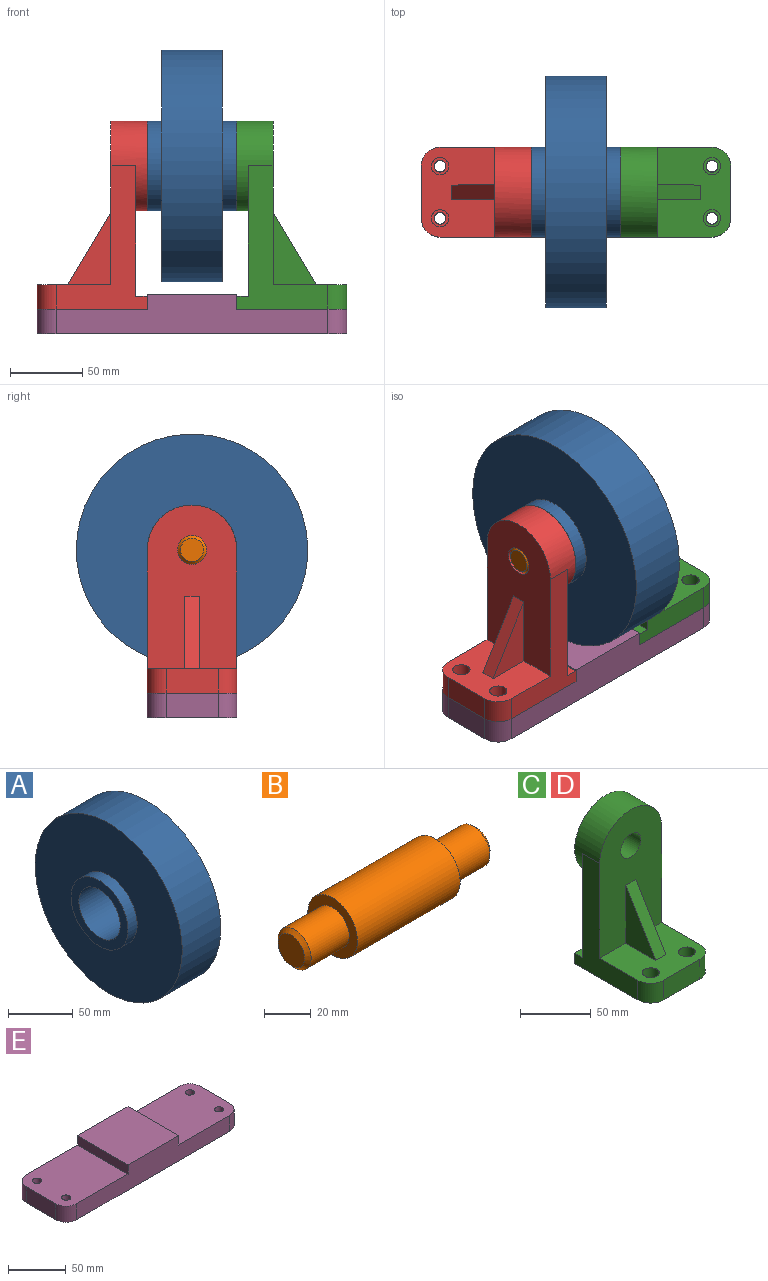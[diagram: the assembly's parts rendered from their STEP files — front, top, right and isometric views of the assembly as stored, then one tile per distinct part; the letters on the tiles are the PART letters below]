
ASSEMBLY  parts=5 mates=4
PART A: 8 faces, bbox 62x160x160 mm
  f0: cylinder r=31mm len=62mm, axis (-1,0,0), area 1947.8mm2, adj f4,f7
  f1: cylinder r=22.5mm len=62mm, axis (-1,0,0), area 8765mm2, adj f3,f4
  f2: cylinder r=31mm len=62mm, axis (-1,0,0), area 1947.8mm2, adj f3,f6
  f3: plane 62x62mm, normal (1,0,0), area 1428.6mm2, adj f1,f2
  f4: plane 62x62mm, normal (-1,0,0), area 1428.6mm2, adj f0,f1
  f5: cylinder r=80mm len=160mm, axis (-1,0,0), area 21111.5mm2, adj f6,f7
  f6: plane 160x160mm, normal (1,0,0), area 17087.1mm2, adj f2,f5
  f7: plane 160x160mm, normal (-1,0,0), area 17087.1mm2, adj f0,f5
PART B: 9 faces, bbox 112x30x30 mm
  f0: cylinder r=10mm len=23mm, axis (-1,0,0), area 1445.1mm2, adj f3,f8
  f1: plane 16x16mm, normal (1,0,0), area 201.1mm2, adj f8
  f2: cylinder r=15mm len=62mm, axis (-1,0,0), area 5843.4mm2, adj f3,f4
  f3: plane 30x30mm, normal (1,0,0), area 392.7mm2, adj f0,f2
  f4: plane 30x30mm, normal (-1,0,0), area 392.7mm2, adj f2,f6
  f5: plane 16x16mm, normal (-1,0,0), area 201.1mm2, adj f7
  f6: cylinder r=10mm len=23mm, axis (-1,0,0), area 1445.1mm2, adj f4,f7
  f7: cone r=10mm half-angle=45deg, axis (1,0,0), area 159.9mm2, adj f5,f6
  f8: cone r=8mm half-angle=45deg, axis (-1,0,0), area 159.9mm2, adj f0,f1
PART C: 23 faces, bbox 62x76x130 mm
  f0: cylinder r=4.1mm len=8.2mm, axis (0,0,-1), area 206.1mm2, adj f9,f17
  f1: cylinder r=4.1mm len=8.2mm, axis (0,0,-1), area 206.1mm2, adj f9,f19
  f2: plane 62x9mm, normal (0,1,0), area 558mm2, adj f3,f7,f9,f11
  f3: plane 99x63mm, normal (-1,0,0), area 2401mm2, adj f2,f4,f8,f9,f10,f11,f12,f14
  f4: cylinder r=13mm len=17mm, axis (0,0,-1), area 347.1mm2, adj f3,f5,f8,f9
  f5: plane 36x17mm, normal (0,-1,0), area 612mm2, adj f4,f6,f8,f9
  f6: cylinder r=13mm len=17mm, axis (0,0,-1), area 347.1mm2, adj f5,f7,f8,f9
  f7: plane 99x63mm, normal (1,0,0), area 2401mm2, adj f2,f6,f8,f9,f10,f11,f12,f14
  f8: plane 62x51mm, normal (0,0,1), area 2563.3mm2, adj f3,f4,f5,f6,f7,f12,f16,f18
  f9: plane 76x62mm, normal (0,0,-1), area 4533.8mm2, adj f0,f1,f2,f3,f4,f5,f6,f7
  f10: plane 90x62mm, normal (0,1,0), area 4070.5mm2, adj f3,f7,f11,f14
  f11: plane 62x8mm, normal (0,0,1), area 496mm2, adj f2,f3,f7,f10
  f12: plane 113x62mm, normal (0,-1,0), area 5779.4mm2, adj f3,f7,f8,f13,f14,f20,f21,f22
  f13: cylinder r=10mm len=25mm, axis (0,-1,0), area 1570.8mm2, adj f12,f15
  f14: cylinder r=31mm len=62mm, axis (0,-1,0), area 3213.8mm2, adj f3,f7,f10,f12,f15
  f15: plane 62x62mm, normal (0,1,0), area 2704.9mm2, adj f13,f14
  f16: cylinder r=6mm len=12mm, axis (0,0,1), area 339.3mm2, adj f8,f17
  f17: plane 12x12mm, normal (0,0,1), area 60.3mm2, adj f0,f16
  f18: cylinder r=6mm len=12mm, axis (0,0,1), area 339.3mm2, adj f8,f19
  f19: plane 12x12mm, normal (0,0,1), area 60.3mm2, adj f1,f18
  f20: plane 50x30mm, normal (-1,0,0), area 750mm2, adj f8,f12,f21
  f21: plane 50x30mm, normal (0,-0.86,0.51), area 583.1mm2, adj f8,f12,f20,f22
  f22: plane 50x30mm, normal (1,0,0), area 750mm2, adj f8,f12,f21
PART D: same geometry as C
PART E: 18 faces, bbox 214x62x27 mm
  f0: plane 188x27mm, normal (0,1,0), area 3816mm2, adj f1,f3,f4,f5,f6,f11,f15,f17
  f1: plane 62x10mm, normal (-1,0,0), area 620mm2, adj f0,f2,f4,f11
  f2: plane 188x27mm, normal (0,-1,0), area 3816mm2, adj f1,f3,f4,f5,f8,f11,f12,f17
  f3: plane 62x10mm, normal (1,0,0), area 620mm2, adj f0,f2,f4,f17
  f4: plane 62x62mm, normal (0,0,1), area 3844mm2, adj f0,f1,f2,f3
  f5: plane 214x62mm, normal (0,0,-1), area 12925mm2, adj f0,f2,f6,f7,f8,f9,f10,f12
  f6: cylinder r=13mm len=17mm, axis (0,0,-1), area 347.1mm2, adj f0,f5,f7,f11
  f7: plane 36x17mm, normal (-1,0,0), area 612mm2, adj f5,f6,f8,f11
  f8: cylinder r=13mm len=17mm, axis (0,0,-1), area 347.1mm2, adj f2,f5,f7,f11
  f9: cylinder r=3.97mm len=17mm, axis (0,0,-1), area 423.9mm2, adj f5,f11
  f10: cylinder r=3.97mm len=17mm, axis (0,0,-1), area 423.9mm2, adj f5,f11
  f11: plane 76x62mm, normal (0,0,1), area 4540.5mm2, adj f0,f1,f2,f6,f7,f8,f9,f10
  f12: cylinder r=13mm len=17mm, axis (0,0,-1), area 347.1mm2, adj f2,f5,f13,f17
  f13: plane 36x17mm, normal (1,0,0), area 612mm2, adj f5,f12,f15,f17
  f14: cylinder r=3.97mm len=17mm, axis (0,0,-1), area 423.9mm2, adj f5,f17
  f15: cylinder r=13mm len=17mm, axis (0,0,-1), area 347.1mm2, adj f0,f5,f13,f17
  f16: cylinder r=3.97mm len=17mm, axis (0,0,-1), area 423.9mm2, adj f5,f17
  f17: plane 76x62mm, normal (0,0,1), area 4540.5mm2, adj f0,f2,f3,f12,f13,f14,f15,f16
PLACE A rot(axis=(-1,0,0),28.9deg) t=(0,0,116)mm
PLACE B t=(0,0,116)mm
PLACE C rot(axis=(0,0,1),90deg) t=(69,0,17)mm
PLACE D rot(axis=(0,0,-1),90deg) t=(-69,0,17)mm
PLACE E at identity fixed
MATE revolute B.f2 <-> A.f5  axis (-1,0,0) through (0,0,116)mm
MATE revolute D.f13 <-> B.f0  axis (-1,0,0) through (-56,0,116)mm
MATE fastened D.f9 <-> E.f11  axis (0,0,-1) through (-107,0,17)mm
MATE fastened C.f9 <-> E.f17  axis (0,0,-1) through (107,0,17)mm
